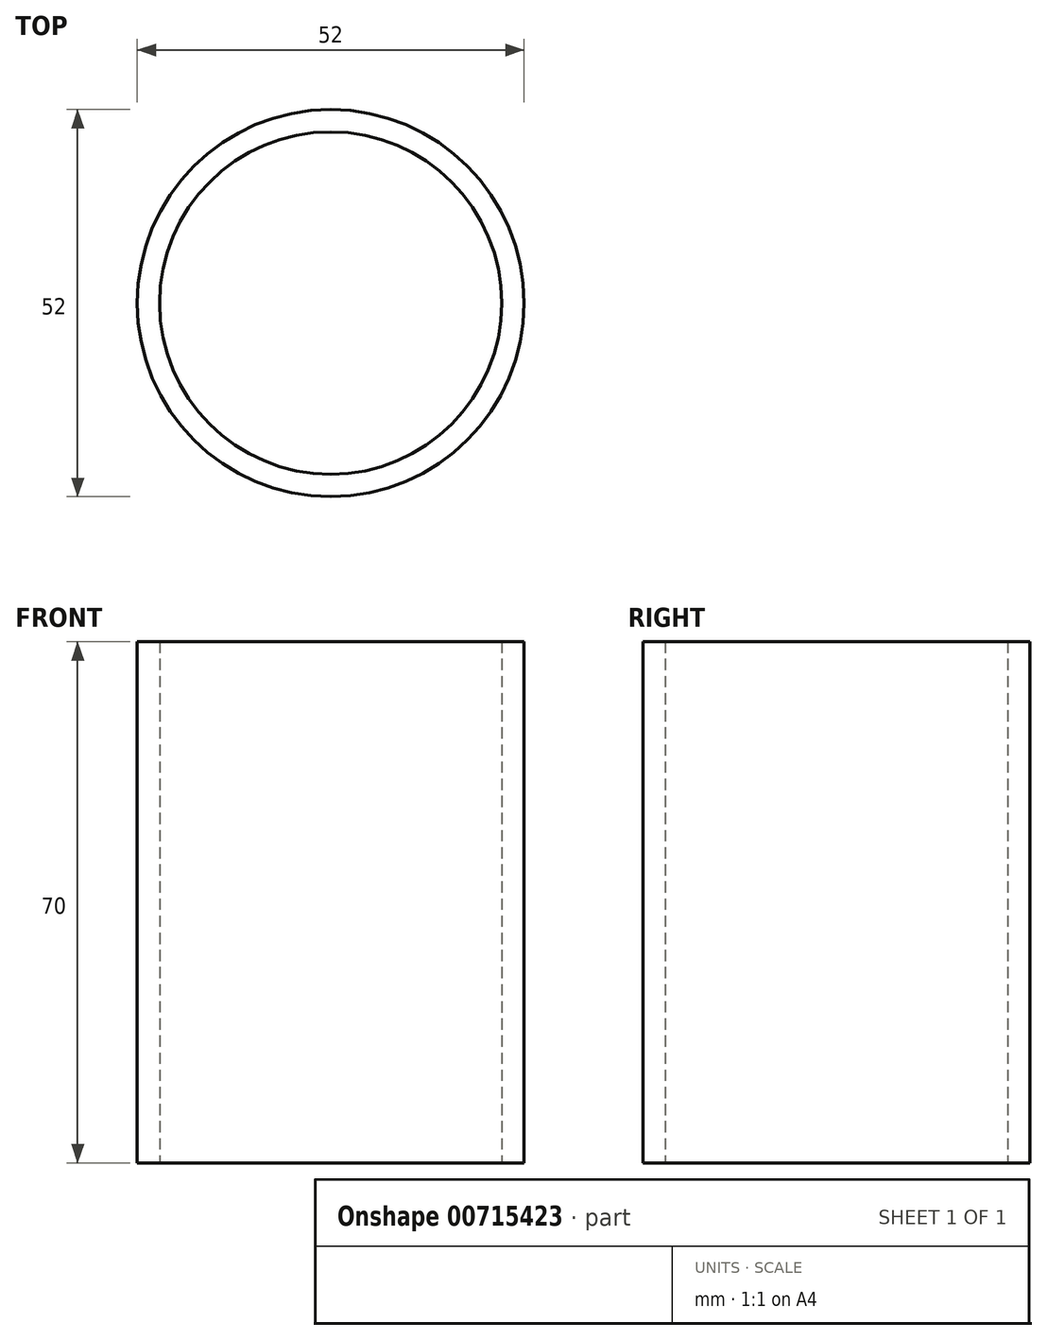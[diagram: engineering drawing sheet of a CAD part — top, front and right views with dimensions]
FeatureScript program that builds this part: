
annotation { "Feature Type Name" : "Feature", "Feature Type Description" : "" }
export const myFeature = defineFeature(function(context is Context, id is Id, definition is map)
    precondition{}
    {
        {
            var Q0;
            Q0=qCreatedBy(makeId("Top.planeOp"),FACE);
            var sketch = newSketch(context, id + "F0", { "sketchPlane" : qUnion([Q0])});
            skCircle(sketch, "E0", {"center": v(0, 0) * mm, "radius": 26 * mm});
            skCircle(sketch, "E1", {"center": v(0, 0) * mm, "radius": 23 * mm});
            skSolve(sketch);
        }
        {
            var Q0;
            Q0=makeQuery(id+"F0.imprint","IMPRINT",FACE,{"disambiguationData":[TD([[makeQuery(id+"F0.imprint","IMPRINT",EDGE,{"derivedFrom":sQuery(id+"F0.wireOp",EDGE,"E0")}),1.0]])]});
            extrude(context, id + "F1", {"entities" : qUnion([Q0]), "depth" : 70 * mm, "offsetDistance" : 25 * mm});
        }
    });
